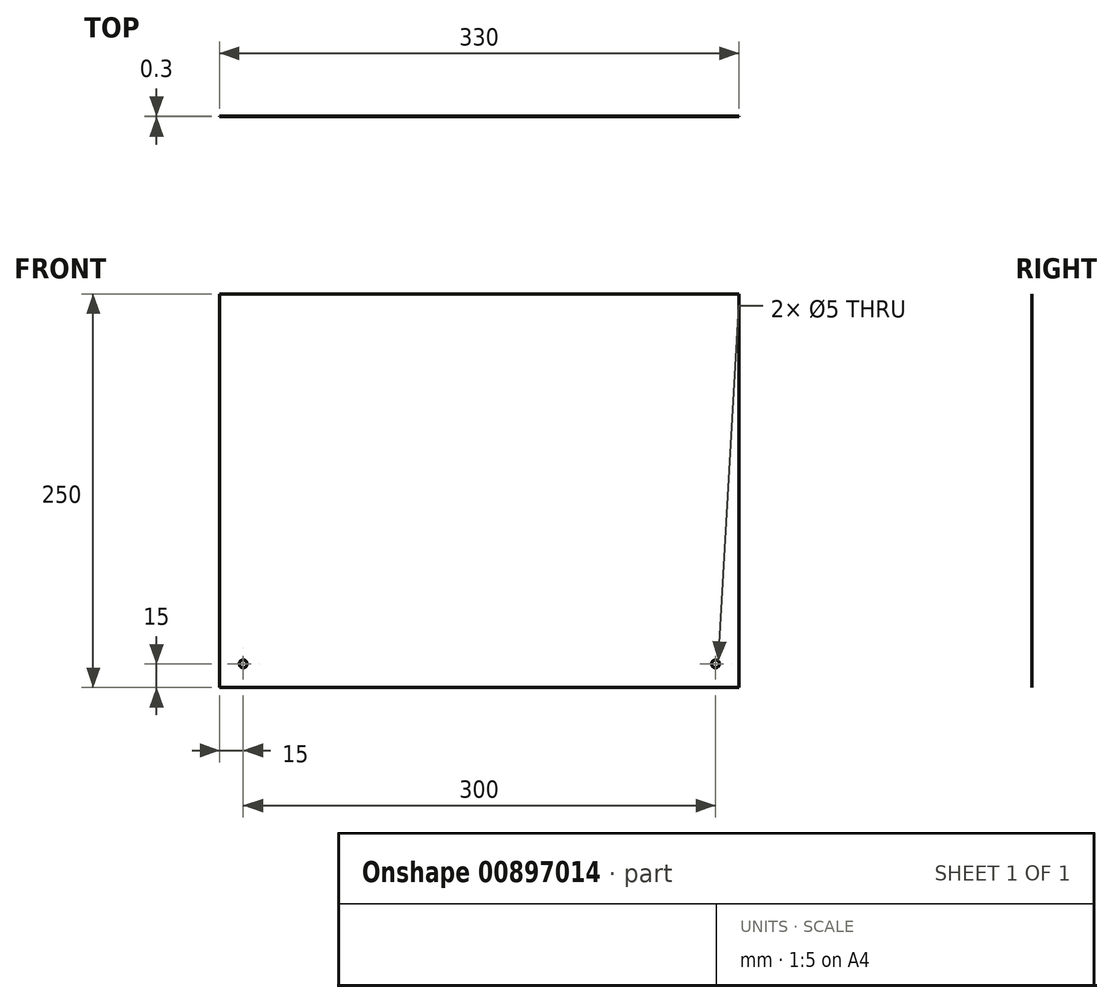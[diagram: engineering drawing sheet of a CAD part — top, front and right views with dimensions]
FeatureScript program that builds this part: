
annotation { "Feature Type Name" : "Feature", "Feature Type Description" : "" }
export const myFeature = defineFeature(function(context is Context, id is Id, definition is map)
    precondition{}
    {
        {
            var Q0;
            Q0=qCreatedBy(makeId("Front.planeOp"),FACE);
            var sketch = newSketch(context, id + "F0", { "sketchPlane" : qUnion([Q0])});
            skLineSegment(sketch, "E0.bottom", {"start": v(0, 0) * mm, "end": v(330, 0) * mm});
            skLineSegment(sketch, "E0.top", {"start": v(0, 250) * mm, "end": v(330, 250) * mm});
            skLineSegment(sketch, "E0.left", {"start": v(0, 0) * mm, "end": v(0, 250) * mm});
            skLineSegment(sketch, "E0.right", {"start": v(330, 0) * mm, "end": v(330, 250) * mm});
            skCircle(sketch, "E1", {"center": v(15, 15) * mm, "radius": 2.5 * mm});
            skCircle(sketch, "E2", {"center": v(315, 15) * mm, "radius": 2.5 * mm});
            skSolve(sketch);
        }
        {
            var Q0;
            Q0 = qSketchRegion(id + "F0", true);
            extrude(context, id + "F1", {"entities" : qUnion([Q0]), "depth" : .3 * mm, "offsetDistance" : 25 * mm});
        }
    });
